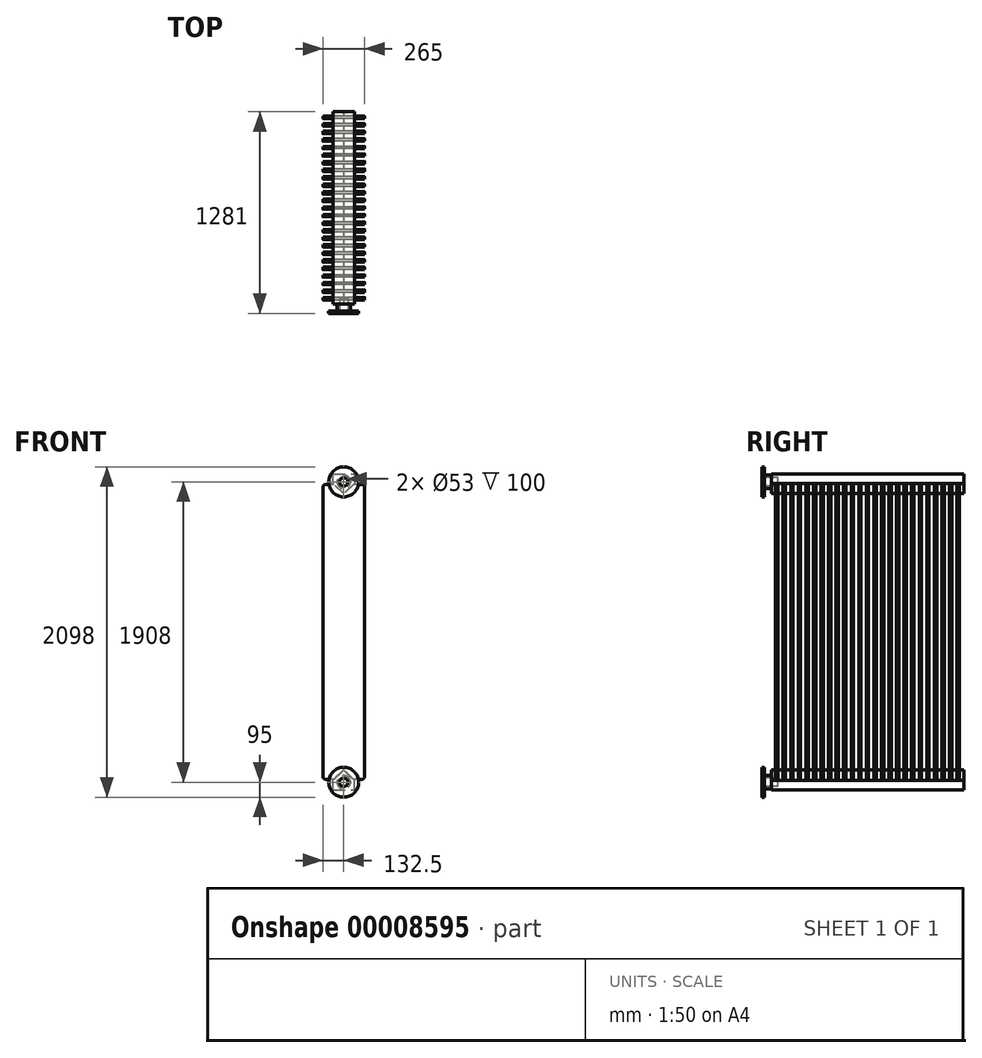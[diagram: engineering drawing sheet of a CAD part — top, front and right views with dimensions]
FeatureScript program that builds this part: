
annotation { "Feature Type Name" : "Feature", "Feature Type Description" : "" }
export const myFeature = defineFeature(function(context is Context, id is Id, definition is map)
    precondition{}
    {
        {
            var Q0;
            Q0=qCreatedBy(makeId("Front.planeOp"),FACE);
            var sketch = newSketch(context, id + "F0", { "sketchPlane" : qUnion([Q0])});
            skLineSegment(sketch, "E0.bottom", {"start": v(0, 0) * mm, "end": v(135, 0) * mm});
            skLineSegment(sketch, "E0.left", {"start": v(0, 0) * mm, "end": v(0, 60) * mm});
            skLineSegment(sketch, "E0.right", {"start": v(135, 0) * mm, "end": v(135, 60) * mm});
            skLineSegment(sketch, "E1", {"start": v(135, 60) * mm, "end": v(67.5, 125) * mm});
            skLineSegment(sketch, "E2", {"start": v(67.5, 125) * mm, "end": v(0, 60) * mm});
            skSolve(sketch);
        }
        {
            var Q0;
            Q0 = qSketchRegion(id + "F0", true);
            extrude(context, id + "F1", {"entities" : qUnion([Q0]), "oppositeDirection" : true, "depth" : 1220 * mm});
        }
        {
            var Q0;
            Q0=qCreatedBy(makeId("Front.planeOp"),FACE);
            cPlane(context, id + "F2", {"entities" : qUnion([Q0]), "cplaneType" : CPlaneType.OFFSET, "offset" : 25 * mm, "oppositeDirection" : true, "width" : 152.4 * mm, "height" : 152.4 * mm});
        }
        {
            var Q0;
            Q0=qCreatedBy(id+"F2.planeOp",FACE);
            var sketch = newSketch(context, id + "F3", { "sketchPlane" : qUnion([Q0])});
            skLineSegment(sketch, "E3.bottom", {"start": v(180, 65) * mm, "end": v(-45, 65) * mm});
            skLineSegment(sketch, "E3.top", {"start": v(180, 1940) * mm, "end": v(-45, 1940) * mm});
            skLineSegment(sketch, "E3.left", {"start": v(200, 85) * mm, "end": v(200, 1920) * mm});
            skLineSegment(sketch, "E3.right", {"start": v(-65, 85) * mm, "end": v(-65, 1920) * mm});
            skPoint(sketch, "E4.visualSharp", {"position": v(-65, 1940) * mm});
            skArc(sketch, "E4.filletArc", {"start": v(-45, 1940) * mm, "mid": v(-59.14, 1934.14) * mm, "end": v(-65, 1920) * mm});
            skPoint(sketch, "E5.visualSharp", {"position": v(200, 1940) * mm});
            skArc(sketch, "E5.filletArc", {"start": v(200, 1920) * mm, "mid": v(194.14, 1934.14) * mm, "end": v(180, 1940) * mm});
            skPoint(sketch, "E6.visualSharp", {"position": v(-65, 65) * mm});
            skArc(sketch, "E6.filletArc", {"start": v(-65, 85) * mm, "mid": v(-59.14, 70.86) * mm, "end": v(-45, 65) * mm});
            skPoint(sketch, "E7.visualSharp", {"position": v(200, 65) * mm});
            skArc(sketch, "E7.filletArc", {"start": v(180, 65) * mm, "mid": v(194.14, 70.86) * mm, "end": v(200, 85) * mm});
            skSolve(sketch);
        }
        {
            var Q0;
            Q0=qCreatedBy(id+"F2.planeOp",FACE);
            cPlane(context, id + "F4", {"entities" : qUnion([Q0]), "cplaneType" : CPlaneType.OFFSET, "offset" : 48 * mm, "oppositeDirection" : true, "width" : 152.4 * mm, "height" : 152.4 * mm});
        }
        {
            var Q0;
            Q0=qCreatedBy(id+"F4.planeOp",FACE);
            var sketch = newSketch(context, id + "F5", { "sketchPlane" : qUnion([Q0])});
            skLineSegment(sketch, "E8.bottom", {"start": v(180, 65) * mm, "end": v(-45, 65) * mm});
            skLineSegment(sketch, "E8.top", {"start": v(180, 1940) * mm, "end": v(-45, 1940) * mm});
            skLineSegment(sketch, "E8.left", {"start": v(200, 85) * mm, "end": v(200, 1920) * mm});
            skLineSegment(sketch, "E8.right", {"start": v(-65, 85) * mm, "end": v(-65, 1920) * mm});
            skPoint(sketch, "E9.visualSharp", {"position": v(-65, 1940) * mm});
            skArc(sketch, "E9.filletArc", {"start": v(-45, 1940) * mm, "mid": v(-59.14, 1934.14) * mm, "end": v(-65, 1920) * mm});
            skPoint(sketch, "E10.visualSharp", {"position": v(200, 1940) * mm});
            skArc(sketch, "E10.filletArc", {"start": v(200, 1920) * mm, "mid": v(194.14, 1934.14) * mm, "end": v(180, 1940) * mm});
            skPoint(sketch, "E11.visualSharp", {"position": v(-65, 65) * mm});
            skArc(sketch, "E11.filletArc", {"start": v(-65, 85) * mm, "mid": v(-59.14, 70.86) * mm, "end": v(-45, 65) * mm});
            skPoint(sketch, "E12.visualSharp", {"position": v(200, 65) * mm});
            skArc(sketch, "E12.filletArc", {"start": v(180, 65) * mm, "mid": v(194.14, 70.86) * mm, "end": v(200, 85) * mm});
            skSolve(sketch);
        }
        {
            var Q0;
            Q0=qCreatedBy(id+"F4.planeOp",FACE);
            cPlane(context, id + "F6", {"entities" : qUnion([Q0]), "cplaneType" : CPlaneType.OFFSET, "offset" : 48 * mm, "oppositeDirection" : true, "width" : 152.4 * mm, "height" : 152.4 * mm});
        }
        {
            var Q0;
            Q0=qCreatedBy(id+"F6.planeOp",FACE);
            var sketch = newSketch(context, id + "F7", { "sketchPlane" : qUnion([Q0])});
            skLineSegment(sketch, "E13.bottom", {"start": v(180, 65) * mm, "end": v(-45, 65) * mm});
            skLineSegment(sketch, "E13.top", {"start": v(180, 1940) * mm, "end": v(-45, 1940) * mm});
            skLineSegment(sketch, "E13.left", {"start": v(200, 85) * mm, "end": v(200, 1920) * mm});
            skLineSegment(sketch, "E13.right", {"start": v(-65, 85) * mm, "end": v(-65, 1920) * mm});
            skPoint(sketch, "E14.visualSharp", {"position": v(-65, 1940) * mm});
            skArc(sketch, "E14.filletArc", {"start": v(-45, 1940) * mm, "mid": v(-59.14, 1934.14) * mm, "end": v(-65, 1920) * mm});
            skPoint(sketch, "E15.visualSharp", {"position": v(200, 1940) * mm});
            skArc(sketch, "E15.filletArc", {"start": v(200, 1920) * mm, "mid": v(194.14, 1934.14) * mm, "end": v(180, 1940) * mm});
            skPoint(sketch, "E16.visualSharp", {"position": v(-65, 65) * mm});
            skArc(sketch, "E16.filletArc", {"start": v(-65, 85) * mm, "mid": v(-59.14, 70.86) * mm, "end": v(-45, 65) * mm});
            skPoint(sketch, "E17.visualSharp", {"position": v(200, 65) * mm});
            skArc(sketch, "E17.filletArc", {"start": v(180, 65) * mm, "mid": v(194.14, 70.86) * mm, "end": v(200, 85) * mm});
            skSolve(sketch);
        }
        {
            var Q0;
            Q0=qCreatedBy(id+"F6.planeOp",FACE);
            cPlane(context, id + "F8", {"entities" : qUnion([Q0]), "cplaneType" : CPlaneType.OFFSET, "offset" : 48 * mm, "oppositeDirection" : true, "width" : 152.4 * mm, "height" : 152.4 * mm});
        }
        {
            var Q0;
            Q0=qCreatedBy(id+"F8.planeOp",FACE);
            var sketch = newSketch(context, id + "F9", { "sketchPlane" : qUnion([Q0])});
            skLineSegment(sketch, "E18.bottom", {"start": v(180, 65) * mm, "end": v(-45, 65) * mm});
            skLineSegment(sketch, "E18.top", {"start": v(180, 1940) * mm, "end": v(-45, 1940) * mm});
            skLineSegment(sketch, "E18.left", {"start": v(200, 85) * mm, "end": v(200, 1920) * mm});
            skLineSegment(sketch, "E18.right", {"start": v(-65, 85) * mm, "end": v(-65, 1920) * mm});
            skPoint(sketch, "E19.visualSharp", {"position": v(-65, 1940) * mm});
            skArc(sketch, "E19.filletArc", {"start": v(-45, 1940) * mm, "mid": v(-59.14, 1934.14) * mm, "end": v(-65, 1920) * mm});
            skPoint(sketch, "E20.visualSharp", {"position": v(200, 1940) * mm});
            skArc(sketch, "E20.filletArc", {"start": v(200, 1920) * mm, "mid": v(194.14, 1934.14) * mm, "end": v(180, 1940) * mm});
            skPoint(sketch, "E21.visualSharp", {"position": v(-65, 65) * mm});
            skArc(sketch, "E21.filletArc", {"start": v(-65, 85) * mm, "mid": v(-59.14, 70.86) * mm, "end": v(-45, 65) * mm});
            skPoint(sketch, "E22.visualSharp", {"position": v(200, 65) * mm});
            skArc(sketch, "E22.filletArc", {"start": v(180, 65) * mm, "mid": v(194.14, 70.86) * mm, "end": v(200, 85) * mm});
            skSolve(sketch);
        }
        {
            var Q0;
            Q0=qCreatedBy(id+"F8.planeOp",FACE);
            cPlane(context, id + "F10", {"entities" : qUnion([Q0]), "cplaneType" : CPlaneType.OFFSET, "offset" : 48 * mm, "oppositeDirection" : true, "width" : 152.4 * mm, "height" : 152.4 * mm});
        }
        {
            var Q0;
            Q0=qCreatedBy(id+"F10.planeOp",FACE);
            var sketch = newSketch(context, id + "F11", { "sketchPlane" : qUnion([Q0])});
            skLineSegment(sketch, "E23.bottom", {"start": v(180, 65) * mm, "end": v(-45, 65) * mm});
            skLineSegment(sketch, "E23.top", {"start": v(180, 1940) * mm, "end": v(-45, 1940) * mm});
            skLineSegment(sketch, "E23.left", {"start": v(200, 85) * mm, "end": v(200, 1920) * mm});
            skLineSegment(sketch, "E23.right", {"start": v(-65, 85) * mm, "end": v(-65, 1920) * mm});
            skPoint(sketch, "E24.visualSharp", {"position": v(-65, 1940) * mm});
            skArc(sketch, "E24.filletArc", {"start": v(-45, 1940) * mm, "mid": v(-59.14, 1934.14) * mm, "end": v(-65, 1920) * mm});
            skPoint(sketch, "E25.visualSharp", {"position": v(200, 1940) * mm});
            skArc(sketch, "E25.filletArc", {"start": v(200, 1920) * mm, "mid": v(194.14, 1934.14) * mm, "end": v(180, 1940) * mm});
            skPoint(sketch, "E26.visualSharp", {"position": v(-65, 65) * mm});
            skArc(sketch, "E26.filletArc", {"start": v(-65, 85) * mm, "mid": v(-59.14, 70.86) * mm, "end": v(-45, 65) * mm});
            skPoint(sketch, "E27.visualSharp", {"position": v(200, 65) * mm});
            skArc(sketch, "E27.filletArc", {"start": v(180, 65) * mm, "mid": v(194.14, 70.86) * mm, "end": v(200, 85) * mm});
            skSolve(sketch);
        }
        {
            var Q0;
            Q0=qCreatedBy(id+"F10.planeOp",FACE);
            cPlane(context, id + "F12", {"entities" : qUnion([Q0]), "cplaneType" : CPlaneType.OFFSET, "offset" : 48 * mm, "oppositeDirection" : true, "width" : 152.4 * mm, "height" : 152.4 * mm});
        }
        {
            var Q0;
            Q0=qCreatedBy(id+"F12.planeOp",FACE);
            var sketch = newSketch(context, id + "F13", { "sketchPlane" : qUnion([Q0])});
            skLineSegment(sketch, "E28.bottom", {"start": v(180, 65) * mm, "end": v(-45, 65) * mm});
            skLineSegment(sketch, "E28.top", {"start": v(180, 1940) * mm, "end": v(-45, 1940) * mm});
            skLineSegment(sketch, "E28.left", {"start": v(200, 85) * mm, "end": v(200, 1920) * mm});
            skLineSegment(sketch, "E28.right", {"start": v(-65, 85) * mm, "end": v(-65, 1920) * mm});
            skPoint(sketch, "E29.visualSharp", {"position": v(-65, 1940) * mm});
            skArc(sketch, "E29.filletArc", {"start": v(-45, 1940) * mm, "mid": v(-59.14, 1934.14) * mm, "end": v(-65, 1920) * mm});
            skPoint(sketch, "E30.visualSharp", {"position": v(200, 1940) * mm});
            skArc(sketch, "E30.filletArc", {"start": v(200, 1920) * mm, "mid": v(194.14, 1934.14) * mm, "end": v(180, 1940) * mm});
            skPoint(sketch, "E31.visualSharp", {"position": v(-65, 65) * mm});
            skArc(sketch, "E31.filletArc", {"start": v(-65, 85) * mm, "mid": v(-59.14, 70.86) * mm, "end": v(-45, 65) * mm});
            skPoint(sketch, "E32.visualSharp", {"position": v(200, 65) * mm});
            skArc(sketch, "E32.filletArc", {"start": v(180, 65) * mm, "mid": v(194.14, 70.86) * mm, "end": v(200, 85) * mm});
            skSolve(sketch);
        }
        {
            var Q0;
            Q0=qCreatedBy(id+"F12.planeOp",FACE);
            cPlane(context, id + "F14", {"entities" : qUnion([Q0]), "cplaneType" : CPlaneType.OFFSET, "offset" : 48 * mm, "oppositeDirection" : true, "width" : 152.4 * mm, "height" : 152.4 * mm});
        }
        {
            var Q0;
            Q0=qCreatedBy(id+"F14.planeOp",FACE);
            cPlane(context, id + "F15", {"entities" : qUnion([Q0]), "cplaneType" : CPlaneType.OFFSET, "offset" : 48 * mm, "oppositeDirection" : true, "width" : 152.4 * mm, "height" : 152.4 * mm});
        }
        {
            var Q0;
            Q0=qCreatedBy(id+"F15.planeOp",FACE);
            var sketch = newSketch(context, id + "F16", { "sketchPlane" : qUnion([Q0])});
            skLineSegment(sketch, "E33.bottom", {"start": v(180, 65) * mm, "end": v(-45, 65) * mm});
            skLineSegment(sketch, "E33.top", {"start": v(180, 1940) * mm, "end": v(-45, 1940) * mm});
            skLineSegment(sketch, "E33.left", {"start": v(200, 85) * mm, "end": v(200, 1920) * mm});
            skLineSegment(sketch, "E33.right", {"start": v(-65, 85) * mm, "end": v(-65, 1920) * mm});
            skPoint(sketch, "E34.visualSharp", {"position": v(-65, 1940) * mm});
            skArc(sketch, "E34.filletArc", {"start": v(-45, 1940) * mm, "mid": v(-59.14, 1934.14) * mm, "end": v(-65, 1920) * mm});
            skPoint(sketch, "E35.visualSharp", {"position": v(200, 1940) * mm});
            skArc(sketch, "E35.filletArc", {"start": v(200, 1920) * mm, "mid": v(194.14, 1934.14) * mm, "end": v(180, 1940) * mm});
            skPoint(sketch, "E36.visualSharp", {"position": v(-65, 65) * mm});
            skArc(sketch, "E36.filletArc", {"start": v(-65, 85) * mm, "mid": v(-59.14, 70.86) * mm, "end": v(-45, 65) * mm});
            skPoint(sketch, "E37.visualSharp", {"position": v(200, 65) * mm});
            skArc(sketch, "E37.filletArc", {"start": v(180, 65) * mm, "mid": v(194.14, 70.86) * mm, "end": v(200, 85) * mm});
            skSolve(sketch);
        }
        {
            var Q0;
            Q0=qCreatedBy(id+"F14.planeOp",FACE);
            var sketch = newSketch(context, id + "F17", { "sketchPlane" : qUnion([Q0])});
            skLineSegment(sketch, "E38.bottom", {"start": v(180, 65) * mm, "end": v(-45, 65) * mm});
            skLineSegment(sketch, "E38.top", {"start": v(180, 1940) * mm, "end": v(-45, 1940) * mm});
            skLineSegment(sketch, "E38.left", {"start": v(200, 85) * mm, "end": v(200, 1920) * mm});
            skLineSegment(sketch, "E38.right", {"start": v(-65, 85) * mm, "end": v(-65, 1920) * mm});
            skPoint(sketch, "E39.visualSharp", {"position": v(-65, 1940) * mm});
            skArc(sketch, "E39.filletArc", {"start": v(-45, 1940) * mm, "mid": v(-59.14, 1934.14) * mm, "end": v(-65, 1920) * mm});
            skPoint(sketch, "E40.visualSharp", {"position": v(200, 1940) * mm});
            skArc(sketch, "E40.filletArc", {"start": v(200, 1920) * mm, "mid": v(194.14, 1934.14) * mm, "end": v(180, 1940) * mm});
            skPoint(sketch, "E41.visualSharp", {"position": v(-65, 65) * mm});
            skArc(sketch, "E41.filletArc", {"start": v(-65, 85) * mm, "mid": v(-59.14, 70.86) * mm, "end": v(-45, 65) * mm});
            skPoint(sketch, "E42.visualSharp", {"position": v(200, 65) * mm});
            skArc(sketch, "E42.filletArc", {"start": v(180, 65) * mm, "mid": v(194.14, 70.86) * mm, "end": v(200, 85) * mm});
            skSolve(sketch);
        }
        {
            var Q0;
            Q0=qCreatedBy(id+"F15.planeOp",FACE);
            cPlane(context, id + "F18", {"entities" : qUnion([Q0]), "cplaneType" : CPlaneType.OFFSET, "offset" : 48 * mm, "oppositeDirection" : true, "width" : 152.4 * mm, "height" : 152.4 * mm});
        }
        {
            var Q0;
            Q0=qCreatedBy(id+"F18.planeOp",FACE);
            cPlane(context, id + "F19", {"entities" : qUnion([Q0]), "cplaneType" : CPlaneType.OFFSET, "offset" : 48 * mm, "oppositeDirection" : true, "width" : 152.4 * mm, "height" : 152.4 * mm});
        }
        {
            var Q0;
            Q0=qCreatedBy(id+"F18.planeOp",FACE);
            var sketch = newSketch(context, id + "F20", { "sketchPlane" : qUnion([Q0])});
            skLineSegment(sketch, "E43.bottom", {"start": v(180, 65) * mm, "end": v(-45, 65) * mm});
            skLineSegment(sketch, "E43.top", {"start": v(180, 1940) * mm, "end": v(-45, 1940) * mm});
            skLineSegment(sketch, "E43.left", {"start": v(200, 85) * mm, "end": v(200, 1920) * mm});
            skLineSegment(sketch, "E43.right", {"start": v(-65, 85) * mm, "end": v(-65, 1920) * mm});
            skPoint(sketch, "E44.visualSharp", {"position": v(-65, 1940) * mm});
            skArc(sketch, "E44.filletArc", {"start": v(-45, 1940) * mm, "mid": v(-59.14, 1934.14) * mm, "end": v(-65, 1920) * mm});
            skPoint(sketch, "E45.visualSharp", {"position": v(200, 1940) * mm});
            skArc(sketch, "E45.filletArc", {"start": v(200, 1920) * mm, "mid": v(194.14, 1934.14) * mm, "end": v(180, 1940) * mm});
            skPoint(sketch, "E46.visualSharp", {"position": v(-65, 65) * mm});
            skArc(sketch, "E46.filletArc", {"start": v(-65, 85) * mm, "mid": v(-59.14, 70.86) * mm, "end": v(-45, 65) * mm});
            skPoint(sketch, "E47.visualSharp", {"position": v(200, 65) * mm});
            skArc(sketch, "E47.filletArc", {"start": v(180, 65) * mm, "mid": v(194.14, 70.86) * mm, "end": v(200, 85) * mm});
            skSolve(sketch);
        }
        {
            var Q0;
            Q0=qCreatedBy(id+"F19.planeOp",FACE);
            var sketch = newSketch(context, id + "F21", { "sketchPlane" : qUnion([Q0])});
            skLineSegment(sketch, "E48.bottom", {"start": v(180, 65) * mm, "end": v(-45, 65) * mm});
            skLineSegment(sketch, "E48.top", {"start": v(180, 1940) * mm, "end": v(-45, 1940) * mm});
            skLineSegment(sketch, "E48.left", {"start": v(200, 85) * mm, "end": v(200, 1920) * mm});
            skLineSegment(sketch, "E48.right", {"start": v(-65, 85) * mm, "end": v(-65, 1920) * mm});
            skPoint(sketch, "E49.visualSharp", {"position": v(-65, 1940) * mm});
            skArc(sketch, "E49.filletArc", {"start": v(-45, 1940) * mm, "mid": v(-59.14, 1934.14) * mm, "end": v(-65, 1920) * mm});
            skPoint(sketch, "E50.visualSharp", {"position": v(200, 1940) * mm});
            skArc(sketch, "E50.filletArc", {"start": v(200, 1920) * mm, "mid": v(194.14, 1934.14) * mm, "end": v(180, 1940) * mm});
            skPoint(sketch, "E51.visualSharp", {"position": v(-65, 65) * mm});
            skArc(sketch, "E51.filletArc", {"start": v(-65, 85) * mm, "mid": v(-59.14, 70.86) * mm, "end": v(-45, 65) * mm});
            skPoint(sketch, "E52.visualSharp", {"position": v(200, 65) * mm});
            skArc(sketch, "E52.filletArc", {"start": v(180, 65) * mm, "mid": v(194.14, 70.86) * mm, "end": v(200, 85) * mm});
            skSolve(sketch);
        }
        {
            var Q0;
            Q0=qCreatedBy(id+"F19.planeOp",FACE);
            cPlane(context, id + "F22", {"entities" : qUnion([Q0]), "cplaneType" : CPlaneType.OFFSET, "offset" : 48 * mm, "oppositeDirection" : true, "width" : 152.4 * mm, "height" : 152.4 * mm});
        }
        {
            var Q0;
            Q0=qCreatedBy(id+"F22.planeOp",FACE);
            var sketch = newSketch(context, id + "F23", { "sketchPlane" : qUnion([Q0])});
            skLineSegment(sketch, "E53.bottom", {"start": v(180, 65) * mm, "end": v(-45, 65) * mm});
            skLineSegment(sketch, "E53.top", {"start": v(180, 1940) * mm, "end": v(-45, 1940) * mm});
            skLineSegment(sketch, "E53.left", {"start": v(200, 85) * mm, "end": v(200, 1920) * mm});
            skLineSegment(sketch, "E53.right", {"start": v(-65, 85) * mm, "end": v(-65, 1920) * mm});
            skPoint(sketch, "E54.visualSharp", {"position": v(-65, 1940) * mm});
            skArc(sketch, "E54.filletArc", {"start": v(-45, 1940) * mm, "mid": v(-59.14, 1934.14) * mm, "end": v(-65, 1920) * mm});
            skPoint(sketch, "E55.visualSharp", {"position": v(200, 1940) * mm});
            skArc(sketch, "E55.filletArc", {"start": v(200, 1920) * mm, "mid": v(194.14, 1934.14) * mm, "end": v(180, 1940) * mm});
            skPoint(sketch, "E56.visualSharp", {"position": v(-65, 65) * mm});
            skArc(sketch, "E56.filletArc", {"start": v(-65, 85) * mm, "mid": v(-59.14, 70.86) * mm, "end": v(-45, 65) * mm});
            skPoint(sketch, "E57.visualSharp", {"position": v(200, 65) * mm});
            skArc(sketch, "E57.filletArc", {"start": v(180, 65) * mm, "mid": v(194.14, 70.86) * mm, "end": v(200, 85) * mm});
            skSolve(sketch);
        }
        {
            var Q0;
            Q0=qCreatedBy(id+"F22.planeOp",FACE);
            cPlane(context, id + "F24", {"entities" : qUnion([Q0]), "cplaneType" : CPlaneType.OFFSET, "offset" : 48 * mm, "oppositeDirection" : true, "width" : 152.4 * mm, "height" : 152.4 * mm});
        }
        {
            var Q0;
            Q0=qCreatedBy(id+"F24.planeOp",FACE);
            var sketch = newSketch(context, id + "F25", { "sketchPlane" : qUnion([Q0])});
            skLineSegment(sketch, "E58.bottom", {"start": v(180, 65) * mm, "end": v(-45, 65) * mm});
            skLineSegment(sketch, "E58.top", {"start": v(180, 1940) * mm, "end": v(-45, 1940) * mm});
            skLineSegment(sketch, "E58.left", {"start": v(200, 85) * mm, "end": v(200, 1920) * mm});
            skLineSegment(sketch, "E58.right", {"start": v(-65, 85) * mm, "end": v(-65, 1920) * mm});
            skPoint(sketch, "E59.visualSharp", {"position": v(-65, 1940) * mm});
            skArc(sketch, "E59.filletArc", {"start": v(-45, 1940) * mm, "mid": v(-59.14, 1934.14) * mm, "end": v(-65, 1920) * mm});
            skPoint(sketch, "E60.visualSharp", {"position": v(200, 1940) * mm});
            skArc(sketch, "E60.filletArc", {"start": v(200, 1920) * mm, "mid": v(194.14, 1934.14) * mm, "end": v(180, 1940) * mm});
            skPoint(sketch, "E61.visualSharp", {"position": v(-65, 65) * mm});
            skArc(sketch, "E61.filletArc", {"start": v(-65, 85) * mm, "mid": v(-59.14, 70.86) * mm, "end": v(-45, 65) * mm});
            skPoint(sketch, "E62.visualSharp", {"position": v(200, 65) * mm});
            skArc(sketch, "E62.filletArc", {"start": v(180, 65) * mm, "mid": v(194.14, 70.86) * mm, "end": v(200, 85) * mm});
            skSolve(sketch);
        }
        {
            var Q0;
            Q0=qCreatedBy(id+"F24.planeOp",FACE);
            cPlane(context, id + "F26", {"entities" : qUnion([Q0]), "cplaneType" : CPlaneType.OFFSET, "offset" : 48 * mm, "oppositeDirection" : true, "width" : 152.4 * mm, "height" : 152.4 * mm});
        }
        {
            var Q0;
            Q0=qCreatedBy(id+"F26.planeOp",FACE);
            var sketch = newSketch(context, id + "F27", { "sketchPlane" : qUnion([Q0])});
            skLineSegment(sketch, "E63.bottom", {"start": v(180, 65) * mm, "end": v(-45, 65) * mm});
            skLineSegment(sketch, "E63.top", {"start": v(180, 1940) * mm, "end": v(-45, 1940) * mm});
            skLineSegment(sketch, "E63.left", {"start": v(200, 85) * mm, "end": v(200, 1920) * mm});
            skLineSegment(sketch, "E63.right", {"start": v(-65, 85) * mm, "end": v(-65, 1920) * mm});
            skPoint(sketch, "E64.visualSharp", {"position": v(-65, 1940) * mm});
            skArc(sketch, "E64.filletArc", {"start": v(-45, 1940) * mm, "mid": v(-59.14, 1934.14) * mm, "end": v(-65, 1920) * mm});
            skPoint(sketch, "E65.visualSharp", {"position": v(200, 1940) * mm});
            skArc(sketch, "E65.filletArc", {"start": v(200, 1920) * mm, "mid": v(194.14, 1934.14) * mm, "end": v(180, 1940) * mm});
            skPoint(sketch, "E66.visualSharp", {"position": v(-65, 65) * mm});
            skArc(sketch, "E66.filletArc", {"start": v(-65, 85) * mm, "mid": v(-59.14, 70.86) * mm, "end": v(-45, 65) * mm});
            skPoint(sketch, "E67.visualSharp", {"position": v(200, 65) * mm});
            skArc(sketch, "E67.filletArc", {"start": v(180, 65) * mm, "mid": v(194.14, 70.86) * mm, "end": v(200, 85) * mm});
            skSolve(sketch);
        }
        {
            var Q0;
            Q0=qCreatedBy(id+"F26.planeOp",FACE);
            cPlane(context, id + "F28", {"entities" : qUnion([Q0]), "cplaneType" : CPlaneType.OFFSET, "offset" : 48 * mm, "oppositeDirection" : true, "width" : 152.4 * mm, "height" : 152.4 * mm});
        }
        {
            var Q0;
            Q0=qCreatedBy(id+"F28.planeOp",FACE);
            var sketch = newSketch(context, id + "F29", { "sketchPlane" : qUnion([Q0])});
            skLineSegment(sketch, "E68.bottom", {"start": v(180, 65) * mm, "end": v(-45, 65) * mm});
            skLineSegment(sketch, "E68.top", {"start": v(180, 1940) * mm, "end": v(-45, 1940) * mm});
            skLineSegment(sketch, "E68.left", {"start": v(200, 85) * mm, "end": v(200, 1920) * mm});
            skLineSegment(sketch, "E68.right", {"start": v(-65, 85) * mm, "end": v(-65, 1920) * mm});
            skPoint(sketch, "E69.visualSharp", {"position": v(-65, 1940) * mm});
            skArc(sketch, "E69.filletArc", {"start": v(-45, 1940) * mm, "mid": v(-59.14, 1934.14) * mm, "end": v(-65, 1920) * mm});
            skPoint(sketch, "E70.visualSharp", {"position": v(200, 1940) * mm});
            skArc(sketch, "E70.filletArc", {"start": v(200, 1920) * mm, "mid": v(194.14, 1934.14) * mm, "end": v(180, 1940) * mm});
            skPoint(sketch, "E71.visualSharp", {"position": v(-65, 65) * mm});
            skArc(sketch, "E71.filletArc", {"start": v(-65, 85) * mm, "mid": v(-59.14, 70.86) * mm, "end": v(-45, 65) * mm});
            skPoint(sketch, "E72.visualSharp", {"position": v(200, 65) * mm});
            skArc(sketch, "E72.filletArc", {"start": v(180, 65) * mm, "mid": v(194.14, 70.86) * mm, "end": v(200, 85) * mm});
            skSolve(sketch);
        }
        {
            var Q0;
            Q0=qCreatedBy(id+"F28.planeOp",FACE);
            cPlane(context, id + "F30", {"entities" : qUnion([Q0]), "cplaneType" : CPlaneType.OFFSET, "offset" : 48 * mm, "oppositeDirection" : true, "width" : 152.4 * mm, "height" : 152.4 * mm});
        }
        {
            var Q0;
            Q0=qCreatedBy(id+"F30.planeOp",FACE);
            var sketch = newSketch(context, id + "F31", { "sketchPlane" : qUnion([Q0])});
            skLineSegment(sketch, "E73.bottom", {"start": v(180, 65) * mm, "end": v(-45, 65) * mm});
            skLineSegment(sketch, "E73.top", {"start": v(180, 1940) * mm, "end": v(-45, 1940) * mm});
            skLineSegment(sketch, "E73.left", {"start": v(200, 85) * mm, "end": v(200, 1920) * mm});
            skLineSegment(sketch, "E73.right", {"start": v(-65, 85) * mm, "end": v(-65, 1920) * mm});
            skPoint(sketch, "E74.visualSharp", {"position": v(-65, 1940) * mm});
            skArc(sketch, "E74.filletArc", {"start": v(-45, 1940) * mm, "mid": v(-59.14, 1934.14) * mm, "end": v(-65, 1920) * mm});
            skPoint(sketch, "E75.visualSharp", {"position": v(200, 1940) * mm});
            skArc(sketch, "E75.filletArc", {"start": v(200, 1920) * mm, "mid": v(194.14, 1934.14) * mm, "end": v(180, 1940) * mm});
            skPoint(sketch, "E76.visualSharp", {"position": v(-65, 65) * mm});
            skArc(sketch, "E76.filletArc", {"start": v(-65, 85) * mm, "mid": v(-59.14, 70.86) * mm, "end": v(-45, 65) * mm});
            skPoint(sketch, "E77.visualSharp", {"position": v(200, 65) * mm});
            skArc(sketch, "E77.filletArc", {"start": v(180, 65) * mm, "mid": v(194.14, 70.86) * mm, "end": v(200, 85) * mm});
            skSolve(sketch);
        }
        {
            var Q0;
            Q0=qCreatedBy(id+"F30.planeOp",FACE);
            cPlane(context, id + "F32", {"entities" : qUnion([Q0]), "cplaneType" : CPlaneType.OFFSET, "offset" : 48 * mm, "oppositeDirection" : true, "width" : 152.4 * mm, "height" : 152.4 * mm});
        }
        {
            var Q0;
            Q0=qCreatedBy(id+"F32.planeOp",FACE);
            var sketch = newSketch(context, id + "F33", { "sketchPlane" : qUnion([Q0])});
            skLineSegment(sketch, "E78.bottom", {"start": v(180, 65) * mm, "end": v(-45, 65) * mm});
            skLineSegment(sketch, "E78.top", {"start": v(180, 1940) * mm, "end": v(-45, 1940) * mm});
            skLineSegment(sketch, "E78.left", {"start": v(200, 85) * mm, "end": v(200, 1920) * mm});
            skLineSegment(sketch, "E78.right", {"start": v(-65, 85) * mm, "end": v(-65, 1920) * mm});
            skPoint(sketch, "E79.visualSharp", {"position": v(-65, 1940) * mm});
            skArc(sketch, "E79.filletArc", {"start": v(-45, 1940) * mm, "mid": v(-59.14, 1934.14) * mm, "end": v(-65, 1920) * mm});
            skPoint(sketch, "E80.visualSharp", {"position": v(200, 1940) * mm});
            skArc(sketch, "E80.filletArc", {"start": v(200, 1920) * mm, "mid": v(194.14, 1934.14) * mm, "end": v(180, 1940) * mm});
            skPoint(sketch, "E81.visualSharp", {"position": v(-65, 65) * mm});
            skArc(sketch, "E81.filletArc", {"start": v(-65, 85) * mm, "mid": v(-59.14, 70.86) * mm, "end": v(-45, 65) * mm});
            skPoint(sketch, "E82.visualSharp", {"position": v(200, 65) * mm});
            skArc(sketch, "E82.filletArc", {"start": v(180, 65) * mm, "mid": v(194.14, 70.86) * mm, "end": v(200, 85) * mm});
            skSolve(sketch);
        }
        {
            var Q0;
            Q0=qCreatedBy(id+"F32.planeOp",FACE);
            cPlane(context, id + "F34", {"entities" : qUnion([Q0]), "cplaneType" : CPlaneType.OFFSET, "offset" : 48 * mm, "oppositeDirection" : true, "width" : 152.4 * mm, "height" : 152.4 * mm});
        }
        {
            var Q0;
            Q0=qCreatedBy(id+"F34.planeOp",FACE);
            var sketch = newSketch(context, id + "F35", { "sketchPlane" : qUnion([Q0])});
            skLineSegment(sketch, "E83.bottom", {"start": v(180, 65) * mm, "end": v(-45, 65) * mm});
            skLineSegment(sketch, "E83.top", {"start": v(180, 1940) * mm, "end": v(-45, 1940) * mm});
            skLineSegment(sketch, "E83.left", {"start": v(200, 85) * mm, "end": v(200, 1920) * mm});
            skLineSegment(sketch, "E83.right", {"start": v(-65, 85) * mm, "end": v(-65, 1920) * mm});
            skPoint(sketch, "E84.visualSharp", {"position": v(-65, 1940) * mm});
            skArc(sketch, "E84.filletArc", {"start": v(-45, 1940) * mm, "mid": v(-59.14, 1934.14) * mm, "end": v(-65, 1920) * mm});
            skPoint(sketch, "E85.visualSharp", {"position": v(200, 1940) * mm});
            skArc(sketch, "E85.filletArc", {"start": v(200, 1920) * mm, "mid": v(194.14, 1934.14) * mm, "end": v(180, 1940) * mm});
            skPoint(sketch, "E86.visualSharp", {"position": v(-65, 65) * mm});
            skArc(sketch, "E86.filletArc", {"start": v(-65, 85) * mm, "mid": v(-59.14, 70.86) * mm, "end": v(-45, 65) * mm});
            skPoint(sketch, "E87.visualSharp", {"position": v(200, 65) * mm});
            skArc(sketch, "E87.filletArc", {"start": v(180, 65) * mm, "mid": v(194.14, 70.86) * mm, "end": v(200, 85) * mm});
            skSolve(sketch);
        }
        {
            var Q0;
            Q0=qCreatedBy(id+"F34.planeOp",FACE);
            cPlane(context, id + "F36", {"entities" : qUnion([Q0]), "cplaneType" : CPlaneType.OFFSET, "offset" : 48 * mm, "oppositeDirection" : true, "width" : 152.4 * mm, "height" : 152.4 * mm});
        }
        {
            var Q0;
            Q0=qCreatedBy(id+"F36.planeOp",FACE);
            cPlane(context, id + "F37", {"entities" : qUnion([Q0]), "cplaneType" : CPlaneType.OFFSET, "offset" : 48 * mm, "oppositeDirection" : true, "width" : 152.4 * mm, "height" : 152.4 * mm});
        }
        {
            var Q0;
            Q0=qCreatedBy(id+"F37.planeOp",FACE);
            cPlane(context, id + "F38", {"entities" : qUnion([Q0]), "cplaneType" : CPlaneType.OFFSET, "offset" : 48 * mm, "oppositeDirection" : true, "width" : 152.4 * mm, "height" : 152.4 * mm});
        }
        {
            var Q0;
            Q0=qCreatedBy(id+"F36.planeOp",FACE);
            var sketch = newSketch(context, id + "F39", { "sketchPlane" : qUnion([Q0])});
            skLineSegment(sketch, "E88.bottom", {"start": v(180, 65) * mm, "end": v(-45, 65) * mm});
            skLineSegment(sketch, "E88.top", {"start": v(180, 1940) * mm, "end": v(-45, 1940) * mm});
            skLineSegment(sketch, "E88.left", {"start": v(200, 85) * mm, "end": v(200, 1920) * mm});
            skLineSegment(sketch, "E88.right", {"start": v(-65, 85) * mm, "end": v(-65, 1920) * mm});
            skPoint(sketch, "E89.visualSharp", {"position": v(-65, 1940) * mm});
            skArc(sketch, "E89.filletArc", {"start": v(-45, 1940) * mm, "mid": v(-59.14, 1934.14) * mm, "end": v(-65, 1920) * mm});
            skPoint(sketch, "E90.visualSharp", {"position": v(200, 1940) * mm});
            skArc(sketch, "E90.filletArc", {"start": v(200, 1920) * mm, "mid": v(194.14, 1934.14) * mm, "end": v(180, 1940) * mm});
            skPoint(sketch, "E91.visualSharp", {"position": v(-65, 65) * mm});
            skArc(sketch, "E91.filletArc", {"start": v(-65, 85) * mm, "mid": v(-59.14, 70.86) * mm, "end": v(-45, 65) * mm});
            skPoint(sketch, "E92.visualSharp", {"position": v(200, 65) * mm});
            skArc(sketch, "E92.filletArc", {"start": v(180, 65) * mm, "mid": v(194.14, 70.86) * mm, "end": v(200, 85) * mm});
            skSolve(sketch);
        }
        {
            var Q0;
            Q0=qCreatedBy(id+"F37.planeOp",FACE);
            var sketch = newSketch(context, id + "F40", { "sketchPlane" : qUnion([Q0])});
            skLineSegment(sketch, "E93.bottom", {"start": v(180, 65) * mm, "end": v(-45, 65) * mm});
            skLineSegment(sketch, "E93.top", {"start": v(180, 1940) * mm, "end": v(-45, 1940) * mm});
            skLineSegment(sketch, "E93.left", {"start": v(200, 85) * mm, "end": v(200, 1920) * mm});
            skLineSegment(sketch, "E93.right", {"start": v(-65, 85) * mm, "end": v(-65, 1920) * mm});
            skPoint(sketch, "E94.visualSharp", {"position": v(-65, 1940) * mm});
            skArc(sketch, "E94.filletArc", {"start": v(-45, 1940) * mm, "mid": v(-59.14, 1934.14) * mm, "end": v(-65, 1920) * mm});
            skPoint(sketch, "E95.visualSharp", {"position": v(200, 1940) * mm});
            skArc(sketch, "E95.filletArc", {"start": v(200, 1920) * mm, "mid": v(194.14, 1934.14) * mm, "end": v(180, 1940) * mm});
            skPoint(sketch, "E96.visualSharp", {"position": v(-65, 65) * mm});
            skArc(sketch, "E96.filletArc", {"start": v(-65, 85) * mm, "mid": v(-59.14, 70.86) * mm, "end": v(-45, 65) * mm});
            skPoint(sketch, "E97.visualSharp", {"position": v(200, 65) * mm});
            skArc(sketch, "E97.filletArc", {"start": v(180, 65) * mm, "mid": v(194.14, 70.86) * mm, "end": v(200, 85) * mm});
            skSolve(sketch);
        }
        {
            var Q0;
            Q0=qCreatedBy(id+"F38.planeOp",FACE);
            var sketch = newSketch(context, id + "F41", { "sketchPlane" : qUnion([Q0])});
            skLineSegment(sketch, "E98.bottom", {"start": v(180, 65) * mm, "end": v(-45, 65) * mm});
            skLineSegment(sketch, "E98.top", {"start": v(180, 1940) * mm, "end": v(-45, 1940) * mm});
            skLineSegment(sketch, "E98.left", {"start": v(200, 85) * mm, "end": v(200, 1920) * mm});
            skLineSegment(sketch, "E98.right", {"start": v(-65, 85) * mm, "end": v(-65, 1920) * mm});
            skPoint(sketch, "E99.visualSharp", {"position": v(-65, 1940) * mm});
            skArc(sketch, "E99.filletArc", {"start": v(-45, 1940) * mm, "mid": v(-59.14, 1934.14) * mm, "end": v(-65, 1920) * mm});
            skPoint(sketch, "E100.visualSharp", {"position": v(200, 1940) * mm});
            skArc(sketch, "E100.filletArc", {"start": v(200, 1920) * mm, "mid": v(194.14, 1934.14) * mm, "end": v(180, 1940) * mm});
            skPoint(sketch, "E101.visualSharp", {"position": v(-65, 65) * mm});
            skArc(sketch, "E101.filletArc", {"start": v(-65, 85) * mm, "mid": v(-59.14, 70.86) * mm, "end": v(-45, 65) * mm});
            skPoint(sketch, "E102.visualSharp", {"position": v(200, 65) * mm});
            skArc(sketch, "E102.filletArc", {"start": v(180, 65) * mm, "mid": v(194.14, 70.86) * mm, "end": v(200, 85) * mm});
            skSolve(sketch);
        }
        {
            var Q0;
            Q0=qCreatedBy(id+"F38.planeOp",FACE);
            cPlane(context, id + "F42", {"entities" : qUnion([Q0]), "cplaneType" : CPlaneType.OFFSET, "offset" : 48 * mm, "oppositeDirection" : true, "width" : 152.4 * mm, "height" : 152.4 * mm});
        }
        {
            var Q0;
            Q0=qCreatedBy(id+"F42.planeOp",FACE);
            cPlane(context, id + "F43", {"entities" : qUnion([Q0]), "cplaneType" : CPlaneType.OFFSET, "offset" : 48 * mm, "oppositeDirection" : true, "width" : 152.4 * mm, "height" : 152.4 * mm});
        }
        {
            var Q0;
            Q0=qCreatedBy(id+"F43.planeOp",FACE);
            cPlane(context, id + "F44", {"entities" : qUnion([Q0]), "cplaneType" : CPlaneType.OFFSET, "offset" : 48 * mm, "oppositeDirection" : true, "width" : 152.4 * mm, "height" : 152.4 * mm});
        }
        {
            var Q0;
            Q0=qCreatedBy(id+"F44.planeOp",FACE);
            cPlane(context, id + "F45", {"entities" : qUnion([Q0]), "cplaneType" : CPlaneType.OFFSET, "offset" : 48 * mm, "oppositeDirection" : true, "width" : 152.4 * mm, "height" : 152.4 * mm});
        }
        {
            var Q0;
            Q0=qCreatedBy(id+"F45.planeOp",FACE);
            cPlane(context, id + "F46", {"entities" : qUnion([Q0]), "cplaneType" : CPlaneType.OFFSET, "offset" : 48 * mm, "oppositeDirection" : true, "width" : 152.4 * mm, "height" : 152.4 * mm});
        }
        {
            var Q0;
            Q0=qCreatedBy(id+"F42.planeOp",FACE);
            var sketch = newSketch(context, id + "F47", { "sketchPlane" : qUnion([Q0])});
            skLineSegment(sketch, "E103.bottom", {"start": v(180, 65) * mm, "end": v(-45, 65) * mm});
            skLineSegment(sketch, "E103.top", {"start": v(180, 1940) * mm, "end": v(-45, 1940) * mm});
            skLineSegment(sketch, "E103.left", {"start": v(200, 85) * mm, "end": v(200, 1920) * mm});
            skLineSegment(sketch, "E103.right", {"start": v(-65, 85) * mm, "end": v(-65, 1920) * mm});
            skPoint(sketch, "E104.visualSharp", {"position": v(-65, 1940) * mm});
            skArc(sketch, "E104.filletArc", {"start": v(-45, 1940) * mm, "mid": v(-59.14, 1934.14) * mm, "end": v(-65, 1920) * mm});
            skPoint(sketch, "E105.visualSharp", {"position": v(200, 1940) * mm});
            skArc(sketch, "E105.filletArc", {"start": v(200, 1920) * mm, "mid": v(194.14, 1934.14) * mm, "end": v(180, 1940) * mm});
            skPoint(sketch, "E106.visualSharp", {"position": v(-65, 65) * mm});
            skArc(sketch, "E106.filletArc", {"start": v(-65, 85) * mm, "mid": v(-59.14, 70.86) * mm, "end": v(-45, 65) * mm});
            skPoint(sketch, "E107.visualSharp", {"position": v(200, 65) * mm});
            skArc(sketch, "E107.filletArc", {"start": v(180, 65) * mm, "mid": v(194.14, 70.86) * mm, "end": v(200, 85) * mm});
            skSolve(sketch);
        }
        {
            var Q0;
            Q0=qCreatedBy(id+"F43.planeOp",FACE);
            var sketch = newSketch(context, id + "F48", { "sketchPlane" : qUnion([Q0])});
            skLineSegment(sketch, "E108.bottom", {"start": v(180, 65) * mm, "end": v(-45, 65) * mm});
            skLineSegment(sketch, "E108.top", {"start": v(180, 1940) * mm, "end": v(-45, 1940) * mm});
            skLineSegment(sketch, "E108.left", {"start": v(200, 85) * mm, "end": v(200, 1920) * mm});
            skLineSegment(sketch, "E108.right", {"start": v(-65, 85) * mm, "end": v(-65, 1920) * mm});
            skPoint(sketch, "E109.visualSharp", {"position": v(-65, 1940) * mm});
            skArc(sketch, "E109.filletArc", {"start": v(-45, 1940) * mm, "mid": v(-59.14, 1934.14) * mm, "end": v(-65, 1920) * mm});
            skPoint(sketch, "E110.visualSharp", {"position": v(200, 1940) * mm});
            skArc(sketch, "E110.filletArc", {"start": v(200, 1920) * mm, "mid": v(194.14, 1934.14) * mm, "end": v(180, 1940) * mm});
            skPoint(sketch, "E111.visualSharp", {"position": v(-65, 65) * mm});
            skArc(sketch, "E111.filletArc", {"start": v(-65, 85) * mm, "mid": v(-59.14, 70.86) * mm, "end": v(-45, 65) * mm});
            skPoint(sketch, "E112.visualSharp", {"position": v(200, 65) * mm});
            skArc(sketch, "E112.filletArc", {"start": v(180, 65) * mm, "mid": v(194.14, 70.86) * mm, "end": v(200, 85) * mm});
            skSolve(sketch);
        }
        {
            var Q0;
            Q0=qCreatedBy(id+"F44.planeOp",FACE);
            var sketch = newSketch(context, id + "F49", { "sketchPlane" : qUnion([Q0])});
            skLineSegment(sketch, "E113.bottom", {"start": v(180, 65) * mm, "end": v(-45, 65) * mm});
            skLineSegment(sketch, "E113.top", {"start": v(180, 1940) * mm, "end": v(-45, 1940) * mm});
            skLineSegment(sketch, "E113.left", {"start": v(200, 85) * mm, "end": v(200, 1920) * mm});
            skLineSegment(sketch, "E113.right", {"start": v(-65, 85) * mm, "end": v(-65, 1920) * mm});
            skPoint(sketch, "E114.visualSharp", {"position": v(-65, 1940) * mm});
            skArc(sketch, "E114.filletArc", {"start": v(-45, 1940) * mm, "mid": v(-59.14, 1934.14) * mm, "end": v(-65, 1920) * mm});
            skPoint(sketch, "E115.visualSharp", {"position": v(200, 1940) * mm});
            skArc(sketch, "E115.filletArc", {"start": v(200, 1920) * mm, "mid": v(194.14, 1934.14) * mm, "end": v(180, 1940) * mm});
            skPoint(sketch, "E116.visualSharp", {"position": v(-65, 65) * mm});
            skArc(sketch, "E116.filletArc", {"start": v(-65, 85) * mm, "mid": v(-59.14, 70.86) * mm, "end": v(-45, 65) * mm});
            skPoint(sketch, "E117.visualSharp", {"position": v(200, 65) * mm});
            skArc(sketch, "E117.filletArc", {"start": v(180, 65) * mm, "mid": v(194.14, 70.86) * mm, "end": v(200, 85) * mm});
            skSolve(sketch);
        }
        {
            var Q0;
            Q0=qCreatedBy(id+"F45.planeOp",FACE);
            var sketch = newSketch(context, id + "F50", { "sketchPlane" : qUnion([Q0])});
            skLineSegment(sketch, "E118.bottom", {"start": v(180, 65) * mm, "end": v(-45, 65) * mm});
            skLineSegment(sketch, "E118.top", {"start": v(180, 1940) * mm, "end": v(-45, 1940) * mm});
            skLineSegment(sketch, "E118.left", {"start": v(200, 85) * mm, "end": v(200, 1920) * mm});
            skLineSegment(sketch, "E118.right", {"start": v(-65, 85) * mm, "end": v(-65, 1920) * mm});
            skPoint(sketch, "E119.visualSharp", {"position": v(-65, 1940) * mm});
            skArc(sketch, "E119.filletArc", {"start": v(-45, 1940) * mm, "mid": v(-59.14, 1934.14) * mm, "end": v(-65, 1920) * mm});
            skPoint(sketch, "E120.visualSharp", {"position": v(200, 1940) * mm});
            skArc(sketch, "E120.filletArc", {"start": v(200, 1920) * mm, "mid": v(194.14, 1934.14) * mm, "end": v(180, 1940) * mm});
            skPoint(sketch, "E121.visualSharp", {"position": v(-65, 65) * mm});
            skArc(sketch, "E121.filletArc", {"start": v(-65, 85) * mm, "mid": v(-59.14, 70.86) * mm, "end": v(-45, 65) * mm});
            skPoint(sketch, "E122.visualSharp", {"position": v(200, 65) * mm});
            skArc(sketch, "E122.filletArc", {"start": v(180, 65) * mm, "mid": v(194.14, 70.86) * mm, "end": v(200, 85) * mm});
            skSolve(sketch);
        }
        {
            var Q0;
            Q0=qCreatedBy(id+"F46.planeOp",FACE);
            var sketch = newSketch(context, id + "F51", { "sketchPlane" : qUnion([Q0])});
            skLineSegment(sketch, "E123.bottom", {"start": v(180, 65) * mm, "end": v(-45, 65) * mm});
            skLineSegment(sketch, "E123.top", {"start": v(180, 1940) * mm, "end": v(-45, 1940) * mm});
            skLineSegment(sketch, "E123.left", {"start": v(200, 85) * mm, "end": v(200, 1920) * mm});
            skLineSegment(sketch, "E123.right", {"start": v(-65, 85) * mm, "end": v(-65, 1920) * mm});
            skPoint(sketch, "E124.visualSharp", {"position": v(-65, 1940) * mm});
            skArc(sketch, "E124.filletArc", {"start": v(-45, 1940) * mm, "mid": v(-59.14, 1934.14) * mm, "end": v(-65, 1920) * mm});
            skPoint(sketch, "E125.visualSharp", {"position": v(200, 1940) * mm});
            skArc(sketch, "E125.filletArc", {"start": v(200, 1920) * mm, "mid": v(194.14, 1934.14) * mm, "end": v(180, 1940) * mm});
            skPoint(sketch, "E126.visualSharp", {"position": v(-65, 65) * mm});
            skArc(sketch, "E126.filletArc", {"start": v(-65, 85) * mm, "mid": v(-59.14, 70.86) * mm, "end": v(-45, 65) * mm});
            skPoint(sketch, "E127.visualSharp", {"position": v(200, 65) * mm});
            skArc(sketch, "E127.filletArc", {"start": v(180, 65) * mm, "mid": v(194.14, 70.86) * mm, "end": v(200, 85) * mm});
            skSolve(sketch);
        }
        {
            var Q0;
            Q0=makeQuery(id+"F3.imprint","IMPRINT",FACE,{"disambiguationData":[TD([[makeQuery(id+"F3.imprint","IMPRINT",EDGE,{"derivedFrom":sQuery(id+"F3.wireOp",EDGE,"E3.bottom")}),-1.0]])]});
            extrude(context, id + "F52", {"entities" : qUnion([Q0]), "operationType" : NewBodyOperationType.ADD, "oppositeDirection" : true, "depth" : 15 * mm});
        }
        {
            var Q0;
            Q0=makeQuery(id+"F5.imprint","IMPRINT",FACE,{"disambiguationData":[TD([[makeQuery(id+"F5.imprint","IMPRINT",EDGE,{"derivedFrom":sQuery(id+"F5.wireOp",EDGE,"E8.bottom")}),-1.0]])]});
            var Q1;
            Q1=makeQuery(id+"F7.imprint","IMPRINT",FACE,{"disambiguationData":[TD([[makeQuery(id+"F7.imprint","IMPRINT",EDGE,{"derivedFrom":sQuery(id+"F7.wireOp",EDGE,"E13.bottom")}),-1.0]])]});
            var Q2;
            Q2=makeQuery(id+"F9.imprint","IMPRINT",FACE,{"disambiguationData":[TD([[makeQuery(id+"F9.imprint","IMPRINT",EDGE,{"derivedFrom":sQuery(id+"F9.wireOp",EDGE,"E18.bottom")}),-1.0]])]});
            var Q3;
            Q3=makeQuery(id+"F11.imprint","IMPRINT",FACE,{"disambiguationData":[TD([[makeQuery(id+"F11.imprint","IMPRINT",EDGE,{"derivedFrom":sQuery(id+"F11.wireOp",EDGE,"E23.bottom")}),-1.0]])]});
            var Q4;
            Q4=makeQuery(id+"F13.imprint","IMPRINT",FACE,{"disambiguationData":[TD([[makeQuery(id+"F13.imprint","IMPRINT",EDGE,{"derivedFrom":sQuery(id+"F13.wireOp",EDGE,"E28.bottom")}),-1.0]])]});
            var Q5;
            Q5=makeQuery(id+"F17.imprint","IMPRINT",FACE,{"disambiguationData":[TD([[makeQuery(id+"F17.imprint","IMPRINT",EDGE,{"derivedFrom":sQuery(id+"F17.wireOp",EDGE,"E38.bottom")}),-1.0]])]});
            var Q6;
            Q6=makeQuery(id+"F16.imprint","IMPRINT",FACE,{"disambiguationData":[TD([[makeQuery(id+"F16.imprint","IMPRINT",EDGE,{"derivedFrom":sQuery(id+"F16.wireOp",EDGE,"E33.bottom")}),-1.0]])]});
            var Q7;
            Q7=makeQuery(id+"F20.imprint","IMPRINT",FACE,{"disambiguationData":[TD([[makeQuery(id+"F20.imprint","IMPRINT",EDGE,{"derivedFrom":sQuery(id+"F20.wireOp",EDGE,"E43.bottom")}),-1.0]])]});
            var Q8;
            Q8=makeQuery(id+"F21.imprint","IMPRINT",FACE,{"disambiguationData":[TD([[makeQuery(id+"F21.imprint","IMPRINT",EDGE,{"derivedFrom":sQuery(id+"F21.wireOp",EDGE,"E48.bottom")}),-1.0]])]});
            var Q9;
            Q9=makeQuery(id+"F23.imprint","IMPRINT",FACE,{"disambiguationData":[TD([[makeQuery(id+"F23.imprint","IMPRINT",EDGE,{"derivedFrom":sQuery(id+"F23.wireOp",EDGE,"E53.bottom")}),-1.0]])]});
            var Q10;
            Q10=makeQuery(id+"F25.imprint","IMPRINT",FACE,{"disambiguationData":[TD([[makeQuery(id+"F25.imprint","IMPRINT",EDGE,{"derivedFrom":sQuery(id+"F25.wireOp",EDGE,"E58.bottom")}),-1.0]])]});
            var Q11;
            Q11=makeQuery(id+"F27.imprint","IMPRINT",FACE,{"disambiguationData":[TD([[makeQuery(id+"F27.imprint","IMPRINT",EDGE,{"derivedFrom":sQuery(id+"F27.wireOp",EDGE,"E63.bottom")}),-1.0]])]});
            var Q12;
            Q12=makeQuery(id+"F29.imprint","IMPRINT",FACE,{"disambiguationData":[TD([[makeQuery(id+"F29.imprint","IMPRINT",EDGE,{"derivedFrom":sQuery(id+"F29.wireOp",EDGE,"E68.bottom")}),-1.0]])]});
            var Q13;
            Q13=makeQuery(id+"F31.imprint","IMPRINT",FACE,{"disambiguationData":[TD([[makeQuery(id+"F31.imprint","IMPRINT",EDGE,{"derivedFrom":sQuery(id+"F31.wireOp",EDGE,"E73.bottom")}),-1.0]])]});
            var Q14;
            Q14=makeQuery(id+"F33.imprint","IMPRINT",FACE,{"disambiguationData":[TD([[makeQuery(id+"F33.imprint","IMPRINT",EDGE,{"derivedFrom":sQuery(id+"F33.wireOp",EDGE,"E78.bottom")}),-1.0]])]});
            var Q15;
            Q15=makeQuery(id+"F35.imprint","IMPRINT",FACE,{"disambiguationData":[TD([[makeQuery(id+"F35.imprint","IMPRINT",EDGE,{"derivedFrom":sQuery(id+"F35.wireOp",EDGE,"E83.bottom")}),-1.0]])]});
            var Q16;
            Q16=makeQuery(id+"F39.imprint","IMPRINT",FACE,{"disambiguationData":[TD([[makeQuery(id+"F39.imprint","IMPRINT",EDGE,{"derivedFrom":sQuery(id+"F39.wireOp",EDGE,"E88.bottom")}),-1.0]])]});
            var Q17;
            Q17=makeQuery(id+"F40.imprint","IMPRINT",FACE,{"disambiguationData":[TD([[makeQuery(id+"F40.imprint","IMPRINT",EDGE,{"derivedFrom":sQuery(id+"F40.wireOp",EDGE,"E93.bottom")}),-1.0]])]});
            var Q18;
            Q18=makeQuery(id+"F41.imprint","IMPRINT",FACE,{"disambiguationData":[TD([[makeQuery(id+"F41.imprint","IMPRINT",EDGE,{"derivedFrom":sQuery(id+"F41.wireOp",EDGE,"E98.bottom")}),-1.0]])]});
            var Q19;
            Q19=makeQuery(id+"F47.imprint","IMPRINT",FACE,{"disambiguationData":[TD([[makeQuery(id+"F47.imprint","IMPRINT",EDGE,{"derivedFrom":sQuery(id+"F47.wireOp",EDGE,"E103.bottom")}),-1.0]])]});
            var Q20;
            Q20=makeQuery(id+"F48.imprint","IMPRINT",FACE,{"disambiguationData":[TD([[makeQuery(id+"F48.imprint","IMPRINT",EDGE,{"derivedFrom":sQuery(id+"F48.wireOp",EDGE,"E108.bottom")}),-1.0]])]});
            var Q21;
            Q21=makeQuery(id+"F49.imprint","IMPRINT",FACE,{"disambiguationData":[TD([[makeQuery(id+"F49.imprint","IMPRINT",EDGE,{"derivedFrom":sQuery(id+"F49.wireOp",EDGE,"E113.bottom")}),-1.0]])]});
            var Q22;
            Q22=makeQuery(id+"F50.imprint","IMPRINT",FACE,{"disambiguationData":[TD([[makeQuery(id+"F50.imprint","IMPRINT",EDGE,{"derivedFrom":sQuery(id+"F50.wireOp",EDGE,"E118.bottom")}),-1.0]])]});
            var Q23;
            Q23=makeQuery(id+"F51.imprint","IMPRINT",FACE,{"disambiguationData":[TD([[makeQuery(id+"F51.imprint","IMPRINT",EDGE,{"derivedFrom":sQuery(id+"F51.wireOp",EDGE,"E123.bottom")}),-1.0]])]});
            extrude(context, id + "F53", {"entities" : qUnion([Q0, Q1, Q2, Q3, Q4, Q5, Q6, Q7, Q8, Q9, Q10, Q11, Q12, Q13, Q14, Q15, Q16, Q17, Q18, Q19, Q20, Q21, Q22, Q23]), "operationType" : NewBodyOperationType.ADD, "oppositeDirection" : true, "depth" : 15 * mm});
        }
        {
            var Q0;
            Q0=makeQuery(id+"F1.opExtrude","CAP_FACE",FACE,{"disambiguationData":[OSD([sQuery(id+"F0.wireOp",EDGE,"E0.bottom"),sQuery(id+"F0.wireOp",EDGE,"E0.left"),sQuery(id+"F0.wireOp",EDGE,"E0.right"),sQuery(id+"F0.wireOp",EDGE,"E1"),sQuery(id+"F0.wireOp",EDGE,"E2")])],"isStart":true});
            var sketch = newSketch(context, id + "F54", { "sketchPlane" : qUnion([Q0])});
            skLineSegment(sketch, "E128", {"start": v(0, 0) * mm, "end": v(0, 2005) * mm});
            skLineSegment(sketch, "E129", {"start": v(0, 2005) * mm, "end": v(135, 2005) * mm});
            skLineSegment(sketch, "E130", {"start": v(135, 2005) * mm, "end": v(135, 1945) * mm});
            skLineSegment(sketch, "E131", {"start": v(135, 1945) * mm, "end": v(67.5, 1880) * mm});
            skLineSegment(sketch, "E132", {"start": v(67.5, 1880) * mm, "end": v(0, 1945) * mm});
            skSolve(sketch);
        }
        {
            var Q0;
            Q0 = qSketchRegion(id + "F54", true);
            extrude(context, id + "F55", {"entities" : qUnion([Q0]), "operationType" : NewBodyOperationType.ADD, "oppositeDirection" : true, "depth" : 1220 * mm});
        }
        {
            var Q0;
            Q0=makeQuery(id+"F55.opExtrude","CAP_FACE",FACE,{"disambiguationData":[OSD([sQuery(id+"F54.wireOp",EDGE,"E128"),sQuery(id+"F54.wireOp",EDGE,"E129"),sQuery(id+"F54.wireOp",EDGE,"E130"),sQuery(id+"F54.wireOp",EDGE,"E131"),sQuery(id+"F54.wireOp",EDGE,"E132")])],"isStart":true});
            var sketch = newSketch(context, id + "F56", { "sketchPlane" : qUnion([Q0])});
            skLineSegment(sketch, "E133", {"start": v(67.5, 2005) * mm, "end": v(67.5, 1880) * mm});
            skLineSegment(sketch, "E134", {"start": v(135, 1945) * mm, "end": v(0, 1945) * mm});
            skCircle(sketch, "E135", {"center": v(67.5, 1955) * mm, "radius": 42.5 * mm});
            skSolve(sketch);
        }
        {
            var Q0;
            Q0 = qSketchRegion(id + "F56", true);
            extrude(context, id + "F57", {"entities" : qUnion([Q0]), "operationType" : NewBodyOperationType.ADD, "depth" : 45 * mm});
        }
        {
            var Q0;
            Q0=makeQuery(id+"F57.opExtrude","CAP_FACE",FACE,{"disambiguationData":[OSD([sQuery(id+"F56.wireOp",EDGE,"E135")])],"isStart":false});
            var sketch = newSketch(context, id + "F58", { "sketchPlane" : qUnion([Q0])});
            skCircle(sketch, "E136", {"center": v(67.5, 1955) * mm, "radius": 95 * mm});
            skSolve(sketch);
        }
        {
            var Q0;
            Q0=makeQuery(id+"F58.imprint","IMPRINT",FACE,{"disambiguationData":[TD([[makeQuery(id+"F58.imprint","IMPRINT",EDGE,{"derivedFrom":makeQuery(id+"F57.opExtrude","CAP_EDGE",EDGE,{"disambiguationData":[OSD([sQuery(id+"F56.wireOp",EDGE,"E135")])],"isStart":false})}),1.0]])]});
            var Q1;
            Q1=makeQuery(id+"F58.imprint","IMPRINT",FACE,{"disambiguationData":[TD([[makeQuery(id+"F58.imprint","IMPRINT",EDGE,{"derivedFrom":sQuery(id+"F58.wireOp",EDGE,"E136")}),1.0]])]});
            extrude(context, id + "F59", {"entities" : qUnion([Q0, Q1]), "operationType" : NewBodyOperationType.ADD, "depth" : 16 * mm});
        }
        {
            var Q0;
            Q0=makeQuery(id+"F59.opExtrude","CAP_FACE",FACE,{"disambiguationData":[OSD([sQuery(id+"F58.wireOp",EDGE,"E136")])],"isStart":false});
            var sketch = newSketch(context, id + "F60", { "sketchPlane" : qUnion([Q0])});
            skCircle(sketch, "E137", {"center": v(67.5, 1955) * mm, "radius": 26.5 * mm});
            skSolve(sketch);
        }
        {
            var Q0;
            Q0=makeQuery(id+"F60.imprint","IMPRINT",FACE,{"disambiguationData":[TD([[makeQuery(id+"F60.imprint","IMPRINT",EDGE,{"derivedFrom":sQuery(id+"F60.wireOp",EDGE,"E137")}),1.0]])]});
            extrude(context, id + "F61", {"entities" : qUnion([Q0]), "operationType" : NewBodyOperationType.REMOVE, "oppositeDirection" : true, "depth" : 100 * mm});
        }
        {
            var Q0;
            Q0=makeQuery(id+"F1.opExtrude","CAP_FACE",FACE,{"disambiguationData":[OSD([sQuery(id+"F0.wireOp",EDGE,"E0.bottom"),sQuery(id+"F0.wireOp",EDGE,"E0.left"),sQuery(id+"F0.wireOp",EDGE,"E0.right"),sQuery(id+"F0.wireOp",EDGE,"E1"),sQuery(id+"F0.wireOp",EDGE,"E2")])],"isStart":true});
            var sketch = newSketch(context, id + "F62", { "sketchPlane" : qUnion([Q0])});
            skCircle(sketch, "E138", {"center": v(67.5, 47) * mm, "radius": 42.5 * mm});
            skSolve(sketch);
        }
        {
            var Q0;
            Q0=makeQuery(id+"F62.imprint","IMPRINT",FACE,{"disambiguationData":[TD([[makeQuery(id+"F62.imprint","IMPRINT",EDGE,{"derivedFrom":sQuery(id+"F62.wireOp",EDGE,"E138")}),1.0]])]});
            extrude(context, id + "F63", {"entities" : qUnion([Q0]), "operationType" : NewBodyOperationType.ADD, "depth" : 45 * mm});
        }
        {
            var Q0;
            Q0=makeQuery(id+"F63.opExtrude","CAP_FACE",FACE,{"disambiguationData":[OSD([sQuery(id+"F62.wireOp",EDGE,"E138")])],"isStart":false});
            var sketch = newSketch(context, id + "F64", { "sketchPlane" : qUnion([Q0])});
            skCircle(sketch, "E139", {"center": v(67.5, 47) * mm, "radius": 95 * mm});
            skSolve(sketch);
        }
        {
            var Q0;
            Q0=makeQuery(id+"F64.imprint","IMPRINT",FACE,{"disambiguationData":[TD([[makeQuery(id+"F64.imprint","IMPRINT",EDGE,{"derivedFrom":makeQuery(id+"F63.opExtrude","CAP_EDGE",EDGE,{"disambiguationData":[OSD([sQuery(id+"F62.wireOp",EDGE,"E138")])],"isStart":false})}),1.0]])]});
            var Q1;
            Q1=makeQuery(id+"F64.imprint","IMPRINT",FACE,{"disambiguationData":[TD([[makeQuery(id+"F64.imprint","IMPRINT",EDGE,{"derivedFrom":sQuery(id+"F64.wireOp",EDGE,"E139")}),1.0]])]});
            extrude(context, id + "F65", {"entities" : qUnion([Q0, Q1]), "operationType" : NewBodyOperationType.ADD, "depth" : 16 * mm});
        }
        {
            var Q0;
            Q0=makeQuery(id+"F65.opExtrude","CAP_FACE",FACE,{"disambiguationData":[OSD([sQuery(id+"F64.wireOp",EDGE,"E139")])],"isStart":false});
            var sketch = newSketch(context, id + "F66", { "sketchPlane" : qUnion([Q0])});
            skCircle(sketch, "E140", {"center": v(67.5, 47) * mm, "radius": 26.5 * mm});
            skSolve(sketch);
        }
        {
            var Q0;
            Q0=makeQuery(id+"F66.imprint","IMPRINT",FACE,{"disambiguationData":[TD([[makeQuery(id+"F66.imprint","IMPRINT",EDGE,{"derivedFrom":sQuery(id+"F66.wireOp",EDGE,"E140")}),1.0]])]});
            extrude(context, id + "F67", {"entities" : qUnion([Q0]), "operationType" : NewBodyOperationType.REMOVE, "oppositeDirection" : true, "depth" : 100 * mm});
        }
    });
